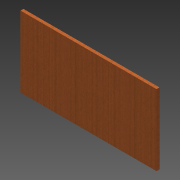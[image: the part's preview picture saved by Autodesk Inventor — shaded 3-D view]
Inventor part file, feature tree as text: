
AUTODESK INVENTOR PART (.ipt)
format: ipt  version: 2013 (Build 170138000, 138)  size: 83,456 bytes
history: native  units: in
note: dims shown in document units (in); Inventor stores cm internally (conversion verified against a paired STEP export)
features: extrude x1, sketch x1
ambient origin geometry x8: Origin, YZ Plane, XZ Plane, XY Plane, X Axis, Y Axis, Z Axis, Center Point
bodies: Solid1 (feature_tree)
feature tree (2):
  extrude  "Extrusion1"  Depth=12.0in
  sketch  "Sketch1"  dims[d0=23.0in d1=12.0in d2=0.5in d3=0.0in]
